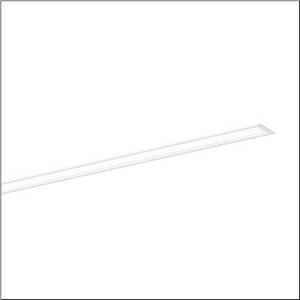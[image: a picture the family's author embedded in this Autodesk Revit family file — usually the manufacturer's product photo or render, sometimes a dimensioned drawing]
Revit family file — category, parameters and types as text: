
# Revit family: silica_r__21_51mx13tctaw_ab10
name_source: partatom
category: Lighting Fixtures
units: mm (PartAtom-declared; Revit-internal decimal feet)

## family parameters
Cut with Voids When Loaded = No
Host = Face
Light Source = No
Part Type = Normal
Room Calculation Point = No
Round Connector Dimension = Use Diameter
Shared = No

## types (1)
- --- (1 x LED, 8070 lm, 81.1 W, 6500K)
    Apparent Load = 81 VA
    CIE Flux Codes = 78 96 99 100 100
    Color Rendering = 80
    Color Temperature = 6500K
    Default Elevation = 1800 mm
    Description = Silica® 21, office luminaire, primary optical cover: prismatic diffuser, of PMMA, CAT 2 (L<= 3000cd/m²), light emission: direct distribution, primary light characteristic: symmetric, installation type: recessed, LED, rated luminous flux: 8.070lm, luminous efficacy: 95lm/W, light colour: 8tw, colour temperature: 2700..6500K, control gear: DALI DT8, with terminal, 3+2-pole, max. 2.5mm², mains connection: 220..240V, AC, 50/60Hz, rated input power: 85.1W, luminaire housing, of aluminium, traffic white (RAL 9016), length: 3.028mm, width: 79mm, height: 53mm, protection rating (complete): IP20, insulation class (complete): insulation class I (protective earthing), certification: CE, ENEC, VDE, permissible operating ambient temperature: 0..+35°C, standard: EN 50419, packaging unit: 1 piece
    Height = 0 mm  [stored 0 ft]
    Lamp = 1 x LED
    Lamp Light Flux = 8070 lm
    Lamp Power = 81.1 W
    Lamp count = 1
    Length = 3027 mm
    Luminous efficacy = 100 lm/W
    Manufacturer = Siteco
    ModVariant = No
    Model = 51MX13TCTAW
    Mounting Place = Ceiling
    Mounting Type = Recessed
    Number of Poles = 1
    OnlyDefault = Yes
    Power Factor = 1
    Product Name = Silica® 21
    Product group = office luminaire | ceiling recessed
    ProductGroupID = 400
    Protection Class = Protection class I
    Protection Degree = IP 20
    RLX_Detail_Level = 1
    RLX_Emergency_Light_Flux = 0 lm
    RLX_Emergency_Type = 0
    RLX_Emergency_Type_DB = No
    RlxData = <blob elided: 13085 chars, md5=646bdfff>
    Socket = socket
    Standby Power = 0 W
    System Light Flux = 8070 lm
    System Power = 81 W
    Type Comments = individual setting
    Type Image = l_1335881.jpg
    URL = http://relux.com
    VarID = @adj_161321
    Voltage = 0 V
    Weight = 0.00 kg
    Width = 79 mm

note: [stored X ft] marks values corroborated as IEEE doubles in the binary element streams (Revit-internal decimal feet)

## geometry (parser evidence)
native form markers: Sweep x9
no freeform markers — native parametric forms only
